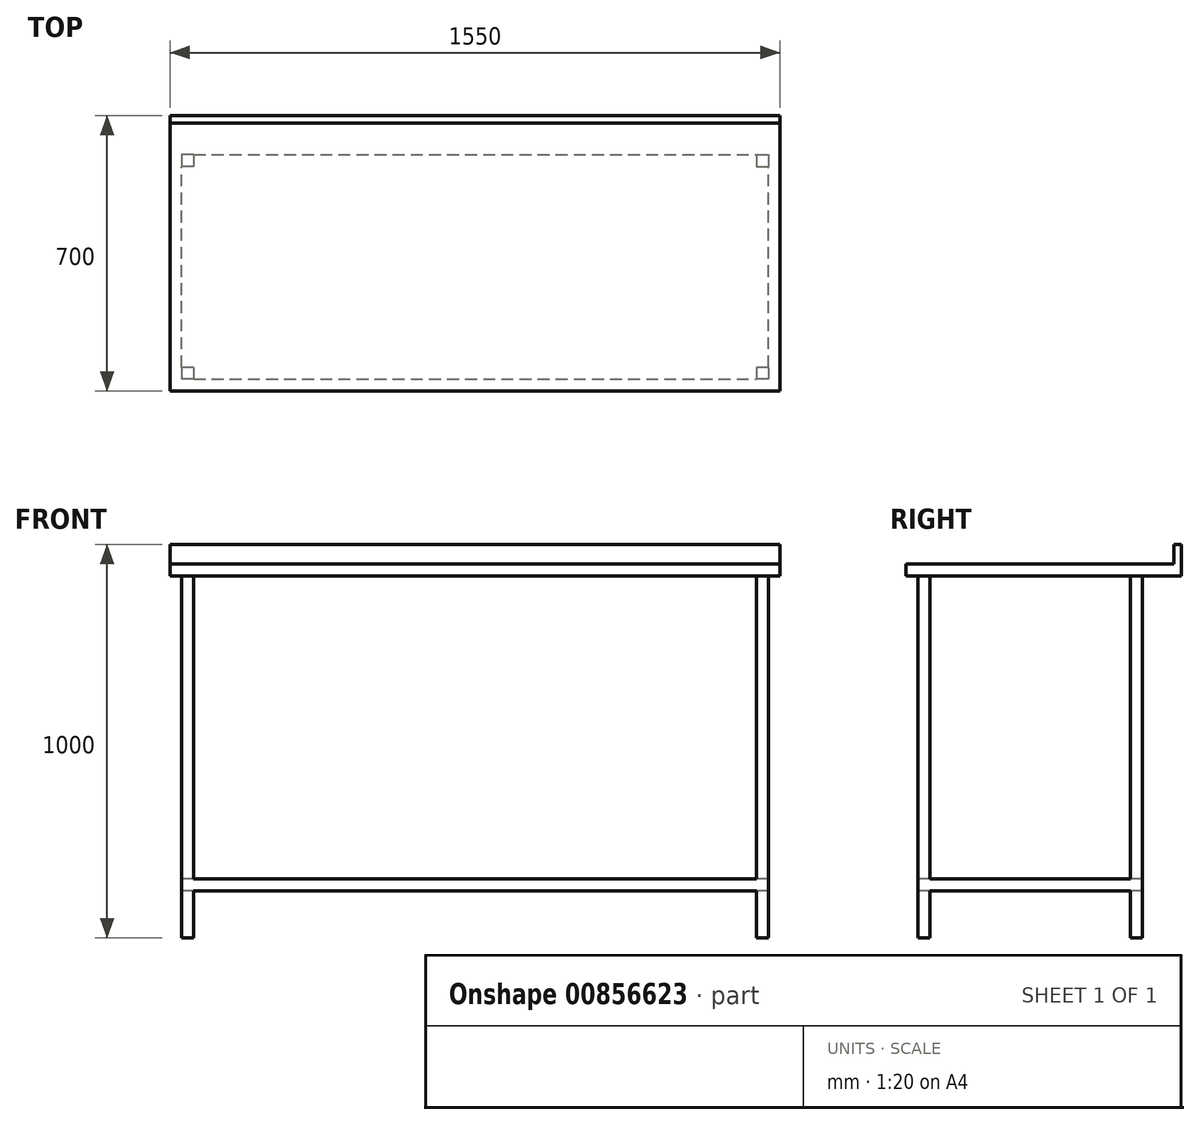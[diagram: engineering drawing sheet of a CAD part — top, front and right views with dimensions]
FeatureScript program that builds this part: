
annotation { "Feature Type Name" : "Feature", "Feature Type Description" : "" }
export const myFeature = defineFeature(function(context is Context, id is Id, definition is map)
    precondition{}
    {
        {
            var Q0;
            Q0=qCreatedBy(makeId("Right.planeOp"),FACE);
            var sketch = newSketch(context, id + "F0", { "sketchPlane" : qUnion([Q0])});
            skLineSegment(sketch, "E0", {"start": v(0, 0) * mm, "end": v(680, 0) * mm});
            skLineSegment(sketch, "E1", {"start": v(680, 0) * mm, "end": v(680, 50) * mm});
            skLineSegment(sketch, "E2", {"start": v(680, 50) * mm, "end": v(700, 50) * mm});
            skLineSegment(sketch, "E3", {"start": v(700, 50) * mm, "end": v(700, -30) * mm});
            skLineSegment(sketch, "E4", {"start": v(700, -30) * mm, "end": v(0, -30) * mm});
            skLineSegment(sketch, "E5", {"start": v(0, -30) * mm, "end": v(0, 0) * mm});
            skSolve(sketch);
        }
        {
            var Q0;
            Q0 = qSketchRegion(id + "F0", true);
            extrude(context, id + "F1", {"entities" : qUnion([Q0]), "depth" : 1550 * mm, "offsetDistance" : 25 * mm});
        }
        {
            var Q0;
            Q0=makeQuery(id+"F1.opExtrude","SWEPT_FACE",FACE,{"disambiguationData":[OSD([sQuery(id+"F0.wireOp",EDGE,"E4")])]});
            var sketch = newSketch(context, id + "F2", { "sketchPlane" : qUnion([Q0])});
            skLineSegment(sketch, "E6.bottom", {"start": v(1520, -60) * mm, "end": v(1490, -60) * mm});
            skLineSegment(sketch, "E6.top", {"start": v(1520, -30) * mm, "end": v(1490, -30) * mm});
            skLineSegment(sketch, "E6.left", {"start": v(1520, -60) * mm, "end": v(1520, -30) * mm});
            skLineSegment(sketch, "E6.right", {"start": v(1490, -60) * mm, "end": v(1490, -30) * mm});
            skPoint(sketch, "E6.middle", {"position": v(1505, -45) * mm});
            skLineSegment(sketch, "E7.bottom", {"start": v(1490, -600) * mm, "end": v(1520, -600) * mm});
            skLineSegment(sketch, "E7.top", {"start": v(1490, -570) * mm, "end": v(1520, -570) * mm});
            skLineSegment(sketch, "E7.left", {"start": v(1490, -600) * mm, "end": v(1490, -570) * mm});
            skLineSegment(sketch, "E7.right", {"start": v(1520, -600) * mm, "end": v(1520, -570) * mm});
            skPoint(sketch, "E7.middle", {"position": v(1505, -585) * mm});
            skLineSegment(sketch, "E8.bottom", {"start": v(60, -600) * mm, "end": v(30, -600) * mm});
            skLineSegment(sketch, "E8.top", {"start": v(60, -570) * mm, "end": v(30, -570) * mm});
            skLineSegment(sketch, "E8.left", {"start": v(60, -600) * mm, "end": v(60, -570) * mm});
            skLineSegment(sketch, "E8.right", {"start": v(30, -600) * mm, "end": v(30, -570) * mm});
            skPoint(sketch, "E8.middle", {"position": v(45, -585) * mm});
            skLineSegment(sketch, "E9.bottom", {"start": v(60, -60) * mm, "end": v(30, -60) * mm});
            skLineSegment(sketch, "E9.top", {"start": v(60, -30) * mm, "end": v(30, -30) * mm});
            skLineSegment(sketch, "E9.left", {"start": v(60, -60) * mm, "end": v(60, -30) * mm});
            skLineSegment(sketch, "E9.right", {"start": v(30, -60) * mm, "end": v(30, -30) * mm});
            skPoint(sketch, "E9.middle", {"position": v(45, -45) * mm});
            skPoint(sketch, "E9.middle.positionSnap0", {"position": v(45, -570) * mm});
            skPoint(sketch, "E9.centerSnap0", {"position": v(45, -570) * mm});
            skSolve(sketch);
        }
        {
            var Q0;
            Q0 = qSketchRegion(id + "F2", true);
            extrude(context, id + "F3", {"entities" : qUnion([Q0]), "operationType" : NewBodyOperationType.ADD, "depth" : 920 * mm, "offsetDistance" : 25 * mm});
        }
        {
            var Q0;
            Q0=makeQuery(id+"F3.opExtrude","SWEPT_FACE",FACE,{"disambiguationData":[OSD([sQuery(id+"F2.wireOp",EDGE,"E6.left")])]});
            var sketch = newSketch(context, id + "F4", { "sketchPlane" : qUnion([Q0])});
            skLineSegment(sketch, "E10.bottom", {"start": v(30, -800) * mm, "end": v(600, -800) * mm});
            skLineSegment(sketch, "E10.top", {"start": v(30, -830) * mm, "end": v(600, -830) * mm});
            skLineSegment(sketch, "E10.left", {"start": v(30, -800) * mm, "end": v(30, -830) * mm});
            skLineSegment(sketch, "E10.right", {"start": v(600, -800) * mm, "end": v(600, -830) * mm});
            skSolve(sketch);
        }
        {
            var Q0;
            Q0 = qSketchRegion(id + "F4", true);
            var Q1;
            Q1=makeQuery(id+"F3.opExtrude","SWEPT_FACE",FACE,{"disambiguationData":[OSD([sQuery(id+"F2.wireOp",EDGE,"E9.right")])]});
            extrude(context, id + "F5", {"entities" : qUnion([Q0]), "operationType" : NewBodyOperationType.ADD, "endBound" : BoundingType.UP_TO_SURFACE, "oppositeDirection" : true, "depth" : 25 * mm, "endBoundEntityFace" : qUnion([Q1]), "offsetDistance" : 25 * mm});
        }
    });
